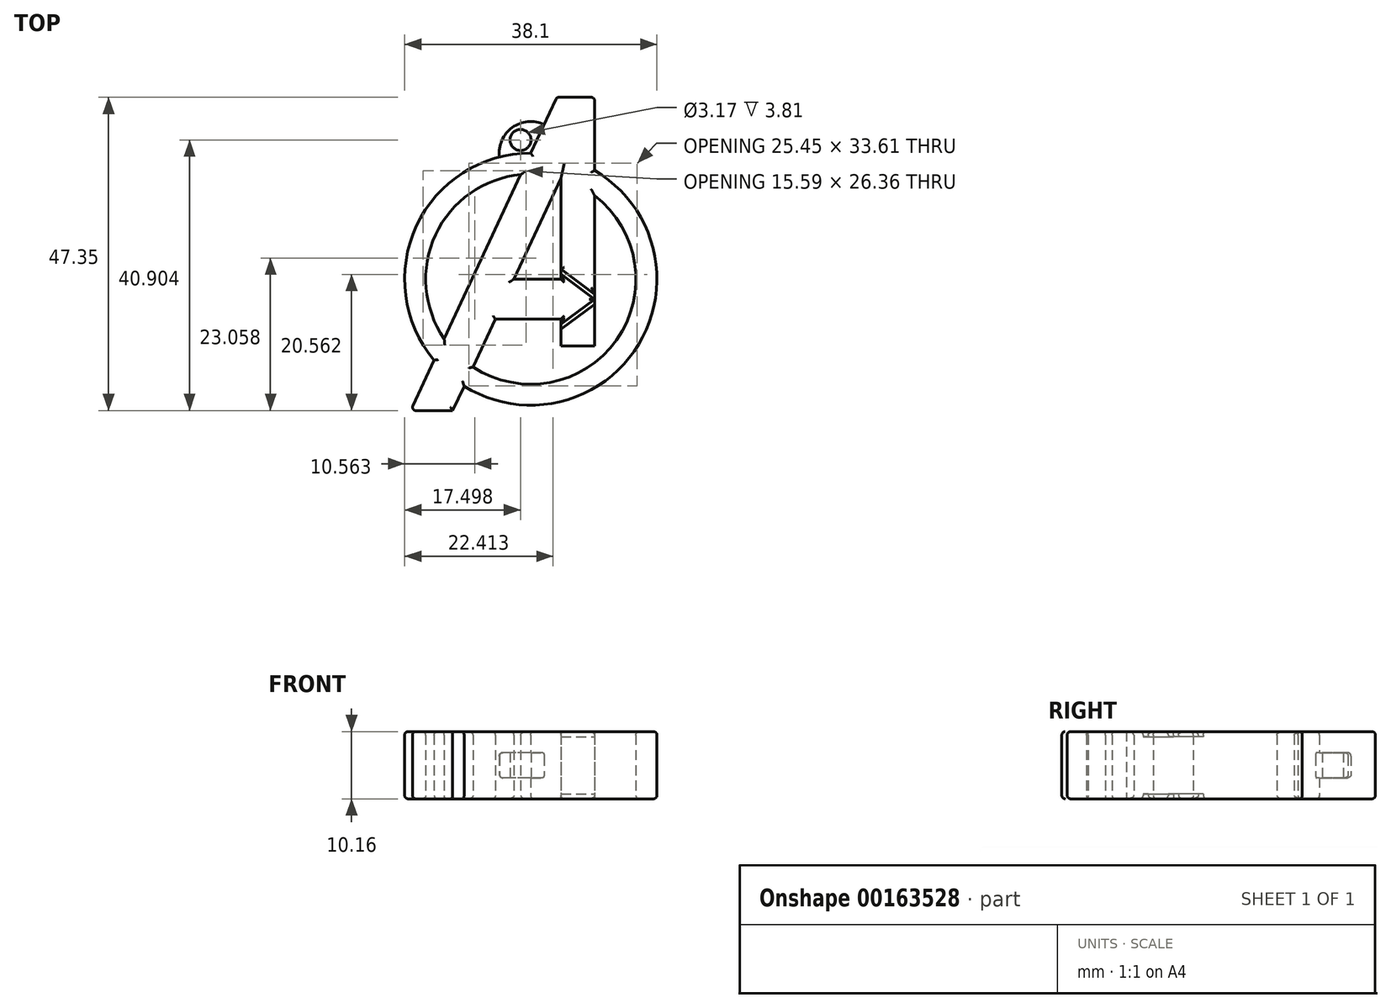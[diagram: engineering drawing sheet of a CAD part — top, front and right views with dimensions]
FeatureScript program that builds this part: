
annotation { "Feature Type Name" : "Feature", "Feature Type Description" : "" }
export const myFeature = defineFeature(function(context is Context, id is Id, definition is map)
    precondition{}
    {
        {
            var Q0;
            Q0=qCreatedBy(makeId("Top.planeOp"),FACE);
            var sketch = newSketch(context, id + "F0", { "sketchPlane" : qUnion([Q0])});
            skArc(sketch, "E0", {"start": v(0, 19.05) * mm, "mid": v(-17.27, 8.05) * mm, "end": v(-14.6, -12.25) * mm});
            skArc(sketch, "E1", {"start": v(-1.51, 15.8) * mm, "mid": v(-14.39, 6.7) * mm, "end": v(-13.08, -9) * mm});
            skLineSegment(sketch, "E2", {"start": v(0, 19.05) * mm, "end": v(-18.15, -19.87) * mm});
            skLineSegment(sketch, "E3", {"start": v(-18.15, -19.87) * mm, "end": v(-11.8, -19.87) * mm});
            skLineSegment(sketch, "E4", {"start": v(-11.8, -19.87) * mm, "end": v(-5.36, -6.05) * mm});
            skLineSegment(sketch, "E5", {"start": v(4.56, 15.2) * mm, "end": v(4.56, 0) * mm});
            skLineSegment(sketch, "E6", {"start": v(4.56, -10.12) * mm, "end": v(9.64, -10.12) * mm});
            skLineSegment(sketch, "E7", {"start": v(-14.6, -12.25) * mm, "end": v(-18.15, -19.87) * mm});
            skLineSegment(sketch, "E8", {"start": v(9.64, 12.61) * mm, "end": v(9.64, 27.48) * mm});
            skLineSegment(sketch, "E9", {"start": v(0, 19.05) * mm, "end": v(3.93, 27.48) * mm});
            skLineSegment(sketch, "E10", {"start": v(9.64, 27.48) * mm, "end": v(3.93, 27.48) * mm});
            skLineSegment(sketch, "E11", {"start": v(-5.36, -6.05) * mm, "end": v(4.56, -6.05) * mm});
            skLineSegment(sketch, "E12", {"start": v(-2.53, 0) * mm, "end": v(4.56, 0) * mm});
            skLineSegment(sketch, "E13.trimOffspring", {"start": v(4.56, -6.05) * mm, "end": v(4.56, -10.12) * mm});
            skLineSegment(sketch, "E14.trimOffspring", {"start": v(-2.53, 0) * mm, "end": v(4.56, 15.2) * mm});
            skArc(sketch, "E15.trimOffspring", {"start": v(-8.72, -13.27) * mm, "mid": v(12.95, -9.18) * mm, "end": v(9.64, 12.61) * mm});
            skArc(sketch, "E16.trimOffspring", {"start": v(-10.07, -16.17) * mm, "mid": v(16.3, -9.86) * mm, "end": v(9.64, 16.43) * mm});
            skArc(sketch, "E17", {"start": v(2.01, 23.37) * mm, "mid": v(-2.8, 22.9) * mm, "end": v(-4.73, 18.45) * mm});
            skCircle(sketch, "E18", {"center": v(-1.55, 21.03) * mm, "radius": 1.59 * mm});
            skLineSegment(sketch, "E19", {"start": v(4.56, 0) * mm, "end": v(4.56, 0.76) * mm});
            skLineSegment(sketch, "E20", {"start": v(4.56, 0.76) * mm, "end": v(4.56, 1.52) * mm});
            skLineSegment(sketch, "E21", {"start": v(4.56, -6.05) * mm, "end": v(4.56, -6.81) * mm});
            skLineSegment(sketch, "E22", {"start": v(4.56, -6.81) * mm, "end": v(4.56, -7.58) * mm});
            skLineSegment(sketch, "E23", {"start": v(4.56, 0.76) * mm, "end": v(9.64, -3.03) * mm});
            skLineSegment(sketch, "E24", {"start": v(4.56, -6.81) * mm, "end": v(9.64, -3.03) * mm});
            skLineSegment(sketch, "E25", {"start": v(4.56, 1.52) * mm, "end": v(9.64, -2.26) * mm});
            skLineSegment(sketch, "E26", {"start": v(4.56, -7.58) * mm, "end": v(9.64, -3.79) * mm});
            skPoint(sketch, "E27.trimOffspring.start.orphan", {"position": v(9.64, -6.05) * mm});
            skPoint(sketch, "E28.end.orphan", {"position": v(9.64, 0) * mm});
            skLineSegment(sketch, "E29", {"start": v(9.64, 12.61) * mm, "end": v(9.64, -10.12) * mm});
            skLineSegment(sketch, "E30", {"start": v(4.56, 1.14) * mm, "end": v(9.64, -2.65) * mm});
            skLineSegment(sketch, "E31", {"start": v(4.56, -7.2) * mm, "end": v(9.64, -3.4) * mm});
            skLineSegment(sketch, "E32", {"start": v(-11.8, -19.87) * mm, "end": v(25.13, -19.87) * mm});
            skLineSegment(sketch, "E33", {"start": v(9.64, 27.48) * mm, "end": v(25.13, 27.48) * mm});
            skLineSegment(sketch, "E34", {"start": v(25.13, 27.48) * mm, "end": v(25.13, -19.87) * mm});
            skLineSegment(sketch, "E35", {"start": v(-19.05, 0) * mm, "end": v(-19.05, -24.18) * mm});
            skLineSegment(sketch, "E36", {"start": v(-19.05, -24.18) * mm, "end": v(19.05, -24.18) * mm});
            skLineSegment(sketch, "E37", {"start": v(19.05, 0) * mm, "end": v(19.05, -24.18) * mm});
            skSolve(sketch);
        }
        {
            var Q0;
            {var subQ2=sQuery(id+"F0.wireOp",EDGE,"E0");Q0=makeQuery(id+"F0.imprint","IMPRINT",FACE,{"disambiguationData":[TD([[makeQuery(id+"F0.imprint","IMPRINT",EDGE,{"derivedFrom":subQ2}),1.0]])]});}
            var Q1;
            {var subQ9=sQuery(id+"F0.wireOp",EDGE,"E3");Q1=makeQuery(id+"F0.imprint","IMPRINT",FACE,{"disambiguationData":[TD([[makeQuery(id+"F0.imprint","IMPRINT",EDGE,{"derivedFrom":subQ9}),1.0]])]});}
            var Q2;
            {var subQ0=sQuery(id+"F0.wireOp",EDGE,"E15.trimOffspring");Q2=makeQuery(id+"F0.imprint","IMPRINT",FACE,{"disambiguationData":[TD([[makeQuery(id+"F0.imprint","IMPRINT",EDGE,{"derivedFrom":subQ0}),-1.0]])]});}
            var Q3;
            Q3=makeQuery(id+"F0.imprint","IMPRINT",FACE,{"disambiguationData":[TD([[makeQuery(id+"F0.imprint","IMPRINT",EDGE,{"derivedFrom":sQuery(id+"F0.wireOp",EDGE,"E6")}),1.0]])]});
            var Q4;
            {var subQ1=sQuery(id+"F0.wireOp",EDGE,"406db947-73c3-418f-ad74-710f48655b45");Q4=makeQuery(id+"F0.imprint","IMPRINT",FACE,{"disambiguationData":[TD([[makeQuery(id+"F0.imprint","IMPRINT",EDGE,{"derivedFrom":subQ1}),-1.0]])]});}
            var Q5;
            {var subQ2=sQuery(id+"F0.wireOp",EDGE,"08405404-7948-4caf-93e0-b9b2559490a3");Q5=makeQuery(id+"F0.imprint","IMPRINT",FACE,{"disambiguationData":[TD([[makeQuery(id+"F0.imprint","IMPRINT",EDGE,{"derivedFrom":subQ2}),1.0]])]});}
            var Q6;
            {var subQ2=sQuery(id+"F0.wireOp",EDGE,"49d6b685-f15b-4148-abe2-4aacc5afd56f");Q6=makeQuery(id+"F0.imprint","IMPRINT",FACE,{"disambiguationData":[TD([[makeQuery(id+"F0.imprint","IMPRINT",EDGE,{"derivedFrom":subQ2}),1.0]])]});}
            var Q7;
            {var subQ2=sQuery(id+"F0.wireOp",EDGE,"e047c4b4-439f-4a13-8362-1945e49fde9b");Q7=makeQuery(id+"F0.imprint","IMPRINT",FACE,{"disambiguationData":[TD([[makeQuery(id+"F0.imprint","IMPRINT",EDGE,{"derivedFrom":subQ2}),1.0]])]});}
            extrude(context, id + "F1", {"entities" : qUnion([Q0, Q1, Q2, Q3, Q4, Q5, Q6, Q7]), "depth" : 5.08 * mm});
        }
        {
            var Q0;
            {var subQ1=sQuery(id+"F0.wireOp",EDGE,"E15.trimOffspring");Q0=makeQuery(id+"F0.imprint","IMPRINT",FACE,{"disambiguationData":[TD([[makeQuery(id+"F0.imprint","IMPRINT",EDGE,{"derivedFrom":subQ1}),-1.0]])]});}
            var Q1;
            {var subQ1=sQuery(id+"F0.wireOp",EDGE,"E1");Q1=makeQuery(id+"F0.imprint","IMPRINT",FACE,{"disambiguationData":[TD([[makeQuery(id+"F0.imprint","IMPRINT",EDGE,{"derivedFrom":subQ1}),-1.0]])]});}
            var Q2;
            {var subQ9=sQuery(id+"F0.wireOp",EDGE,"E3");Q2=makeQuery(id+"F0.imprint","IMPRINT",FACE,{"disambiguationData":[TD([[makeQuery(id+"F0.imprint","IMPRINT",EDGE,{"derivedFrom":subQ9}),1.0]])]});}
            var Q3;
            {var subQ2=sQuery(id+"F0.wireOp",EDGE,"E6");Q3=makeQuery(id+"F0.imprint","IMPRINT",FACE,{"disambiguationData":[TD([[makeQuery(id+"F0.imprint","IMPRINT",EDGE,{"derivedFrom":subQ2}),1.0]])]});}
            extrude(context, id + "F2", {"entities" : qUnion([Q0, Q1, Q2, Q3]), "operationType" : NewBodyOperationType.ADD, "oppositeDirection" : true, "depth" : 5.08 * mm});
        }
        {
            var Q0;
            {var subQ0=sQuery(id+"F0.wireOp",EDGE,"E17");Q0=makeQuery(id+"F0.imprint","IMPRINT",FACE,{"disambiguationData":[TD([[makeQuery(id+"F0.imprint","IMPRINT",EDGE,{"derivedFrom":subQ0}),1.0]])]});}
            extrude(context, id + "F3", {"entities" : qUnion([Q0]), "operationType" : NewBodyOperationType.ADD, "depth" : 1.9 * mm});
        }
        {
            var Q0;
            {var subQ0=sQuery(id+"F0.wireOp",EDGE,"E17");Q0=makeQuery(id+"F0.imprint","IMPRINT",FACE,{"disambiguationData":[TD([[makeQuery(id+"F0.imprint","IMPRINT",EDGE,{"derivedFrom":subQ0}),1.0]])]});}
            extrude(context, id + "F4", {"entities" : qUnion([Q0]), "operationType" : NewBodyOperationType.ADD, "oppositeDirection" : true, "depth" : 1.9 * mm});
        }
        {
            var Q0;
            {var subQ2=sQuery(id+"F0.wireOp",EDGE,"E25");Q0=makeQuery(id+"F0.imprint","IMPRINT",FACE,{"disambiguationData":[TD([[makeQuery(id+"F0.imprint","IMPRINT",EDGE,{"derivedFrom":subQ2}),-1.0]])]});}
            var Q1;
            {var subQ2=sQuery(id+"F0.wireOp",EDGE,"E23");Q1=makeQuery(id+"F0.imprint","IMPRINT",FACE,{"disambiguationData":[TD([[makeQuery(id+"F0.imprint","IMPRINT",EDGE,{"derivedFrom":subQ2}),1.0]])]});}
            var Q2;
            {var subQ2=sQuery(id+"F0.wireOp",EDGE,"E24");Q2=makeQuery(id+"F0.imprint","IMPRINT",FACE,{"disambiguationData":[TD([[makeQuery(id+"F0.imprint","IMPRINT",EDGE,{"derivedFrom":subQ2}),-1.0]])]});}
            var Q3;
            {var subQ2=sQuery(id+"F0.wireOp",EDGE,"E26");Q3=makeQuery(id+"F0.imprint","IMPRINT",FACE,{"disambiguationData":[TD([[makeQuery(id+"F0.imprint","IMPRINT",EDGE,{"derivedFrom":subQ2}),1.0]])]});}
            extrude(context, id + "F5", {"entities" : qUnion([Q0, Q1, Q2, Q3]), "operationType" : NewBodyOperationType.ADD, "depth" : 4.32 * mm});
        }
        {
            var Q0;
            {var subQ2=sQuery(id+"F0.wireOp",EDGE,"E23");Q0=makeQuery(id+"F0.imprint","IMPRINT",FACE,{"disambiguationData":[TD([[makeQuery(id+"F0.imprint","IMPRINT",EDGE,{"derivedFrom":subQ2}),1.0]])]});}
            var Q1;
            {var subQ2=sQuery(id+"F0.wireOp",EDGE,"E25");Q1=makeQuery(id+"F0.imprint","IMPRINT",FACE,{"disambiguationData":[TD([[makeQuery(id+"F0.imprint","IMPRINT",EDGE,{"derivedFrom":subQ2}),-1.0]])]});}
            var Q2;
            {var subQ2=sQuery(id+"F0.wireOp",EDGE,"E24");Q2=makeQuery(id+"F0.imprint","IMPRINT",FACE,{"disambiguationData":[TD([[makeQuery(id+"F0.imprint","IMPRINT",EDGE,{"derivedFrom":subQ2}),-1.0]])]});}
            var Q3;
            {var subQ2=sQuery(id+"F0.wireOp",EDGE,"E26");Q3=makeQuery(id+"F0.imprint","IMPRINT",FACE,{"disambiguationData":[TD([[makeQuery(id+"F0.imprint","IMPRINT",EDGE,{"derivedFrom":subQ2}),1.0]])]});}
            extrude(context, id + "F6", {"entities" : qUnion([Q0, Q1, Q2, Q3]), "operationType" : NewBodyOperationType.ADD, "oppositeDirection" : true, "depth" : 4.32 * mm});
        }
        {
            var Q0;
            Q0=makeQuery(id+"F3.opExtrude","CAP_EDGE",EDGE,{"disambiguationData":[OSD([sQuery(id+"F0.wireOp",EDGE,"E17")])],"isStart":false});
            var Q1;
            Q1=makeQuery(id+"F4.opExtrude","CAP_EDGE",EDGE,{"disambiguationData":[OSD([sQuery(id+"F0.wireOp",EDGE,"E17")])],"isStart":false});
            var Q2;
            Q2=makeQuery(id+"F2.opExtrude","CAP_EDGE",EDGE,{"disambiguationData":[OSD([sQuery(id+"F0.wireOp",EDGE,"E9")])],"isStart":false});
            var Q3;
            Q3=makeQuery(id+"F1.opExtrude","CAP_EDGE",EDGE,{"disambiguationData":[OSD([sQuery(id+"F0.wireOp",EDGE,"E9")])],"isStart":false});
            var Q4;
            Q4=makeQuery(id+"F2.opExtrude","CAP_EDGE",EDGE,{"disambiguationData":[OSD([sQuery(id+"F0.wireOp",EDGE,"E0")])],"isStart":false});
            var Q5;
            Q5=makeQuery(id+"F1.opExtrude","CAP_EDGE",EDGE,{"disambiguationData":[OSD([sQuery(id+"F0.wireOp",EDGE,"E0")])],"isStart":false});
            var Q6;
            Q6=makeQuery(id+"F2.opExtrude","CAP_EDGE",EDGE,{"disambiguationData":[OSD([sQuery(id+"F0.wireOp",EDGE,"E7")])],"isStart":false});
            var Q7;
            Q7=makeQuery(id+"F1.opExtrude","CAP_EDGE",EDGE,{"disambiguationData":[OSD([sQuery(id+"F0.wireOp",EDGE,"E7")])],"isStart":false});
            var Q8;
            {var subQ0=sQuery(id+"F0.wireOp",EDGE,"E3");var subQ1=sQuery(id+"F0.wireOp",EDGE,"E7");Q8=makeQuery(id+"F2.boolean.opBoolean","MERGE",EDGE,{"derivedFrom":[makeQuery(id+"F1.opExtrude","SWEPT_EDGE",EDGE,{"disambiguationData":[OSD([subQ0,subQ1])]}),makeQuery(id+"F2.opExtrude","SWEPT_EDGE",EDGE,{"disambiguationData":[OSD([subQ0,subQ1])]})]});}
            var Q9;
            Q9=makeQuery(id+"F1.opExtrude","CAP_EDGE",EDGE,{"disambiguationData":[OSD([sQuery(id+"F0.wireOp",EDGE,"E3")])],"isStart":false});
            var Q10;
            {var subQ0=sQuery(id+"F0.wireOp",EDGE,"E3");var subQ1=sQuery(id+"F0.wireOp",EDGE,"E4");Q10=makeQuery(id+"F2.boolean.opBoolean","MERGE",EDGE,{"derivedFrom":[makeQuery(id+"F1.opExtrude","SWEPT_EDGE",EDGE,{"disambiguationData":[OSD([subQ0,subQ1])]}),makeQuery(id+"F2.opExtrude","SWEPT_EDGE",EDGE,{"disambiguationData":[OSD([subQ0,subQ1])]})]});}
            var Q11;
            Q11=makeQuery(id+"F2.opExtrude","CAP_EDGE",EDGE,{"disambiguationData":[OSD([sQuery(id+"F0.wireOp",EDGE,"E3")])],"isStart":false});
            var Q12;
            {var subQ0=sQuery(id+"F0.wireOp",EDGE,"E4");Q12=makeQuery(id+"F2.opExtrude","CAP_EDGE",EDGE,{"disambiguationData":[OSD([subQ0]),TDD([makeQuery(id+"F0.imprint","IMPRINT",EDGE,{"disambiguationData":[TD([[makeQuery(id+"F0.imprint","INTERSECT",VERTEX,{"derivedFrom":[sQuery(id+"F0.wireOp",EDGE,"E3"),subQ0]}),-1.0]])],"derivedFrom":subQ0})])],"isStart":false});}
            var Q13;
            {var subQ0=sQuery(id+"F0.wireOp",EDGE,"E4");Q13=makeQuery(id+"F1.opExtrude","CAP_EDGE",EDGE,{"disambiguationData":[OSD([subQ0]),TDD([makeQuery(id+"F0.imprint","IMPRINT",EDGE,{"disambiguationData":[TD([[makeQuery(id+"F0.imprint","INTERSECT",VERTEX,{"derivedFrom":[sQuery(id+"F0.wireOp",EDGE,"E3"),subQ0]}),-1.0]])],"derivedFrom":subQ0})])],"isStart":false});}
            var Q14;
            Q14=makeQuery(id+"F1.opExtrude","CAP_EDGE",EDGE,{"disambiguationData":[OSD([sQuery(id+"F0.wireOp",EDGE,"E16.trimOffspring")])],"isStart":false});
            var Q15;
            Q15=makeQuery(id+"F2.opExtrude","CAP_FACE",FACE,{"disambiguationData":[OSD([sQuery(id+"F0.wireOp",EDGE,"E0"),sQuery(id+"F0.wireOp",EDGE,"E1"),sQuery(id+"F0.wireOp",EDGE,"E2"),sQuery(id+"F0.wireOp",EDGE,"E3"),sQuery(id+"F0.wireOp",EDGE,"E5"),sQuery(id+"F0.wireOp",EDGE,"E7"),sQuery(id+"F0.wireOp",EDGE,"E8"),sQuery(id+"F0.wireOp",EDGE,"E9"),sQuery(id+"F0.wireOp",EDGE,"E10"),sQuery(id+"F0.wireOp",EDGE,"E4"),sQuery(id+"F0.wireOp",EDGE,"E11"),sQuery(id+"F0.wireOp",EDGE,"E12"),sQuery(id+"F0.wireOp",EDGE,"E14.trimOffspring"),sQuery(id+"F0.wireOp",EDGE,"E15.trimOffspring"),sQuery(id+"F0.wireOp",EDGE,"E16.trimOffspring"),sQuery(id+"F0.wireOp",EDGE,"E19"),sQuery(id+"F0.wireOp",EDGE,"E21"),sQuery(id+"F0.wireOp",EDGE,"E23"),sQuery(id+"F0.wireOp",EDGE,"E24"),sQuery(id+"F0.wireOp",EDGE,"E25"),sQuery(id+"F0.wireOp",EDGE,"E29")])],"isStart":false});
            var Q16;
            Q16=makeQuery(id+"F2.opExtrude","CAP_EDGE",EDGE,{"disambiguationData":[OSD([sQuery(id+"F0.wireOp",EDGE,"E16.trimOffspring")])],"isStart":false});
            var Q17;
            {var subQ0=sQuery(id+"F0.wireOp",EDGE,"E8");var subQ1=sQuery(id+"F0.wireOp",EDGE,"E10");Q17=makeQuery(id+"F2.boolean.opBoolean","MERGE",EDGE,{"derivedFrom":[makeQuery(id+"F1.opExtrude","SWEPT_EDGE",EDGE,{"disambiguationData":[OSD([subQ0,subQ1])]}),makeQuery(id+"F2.opExtrude","SWEPT_EDGE",EDGE,{"disambiguationData":[OSD([subQ0,subQ1])]})]});}
            var Q18;
            Q18=makeQuery(id+"F2.opExtrude","CAP_EDGE",EDGE,{"disambiguationData":[OSD([sQuery(id+"F0.wireOp",EDGE,"E8")])],"isStart":false});
            var Q19;
            Q19=makeQuery(id+"F1.opExtrude","CAP_EDGE",EDGE,{"disambiguationData":[OSD([sQuery(id+"F0.wireOp",EDGE,"E8")])],"isStart":false});
            var Q20;
            {var subQ0=sQuery(id+"F0.wireOp",EDGE,"E9");var subQ1=sQuery(id+"F0.wireOp",EDGE,"E10");Q20=makeQuery(id+"F2.boolean.opBoolean","MERGE",EDGE,{"derivedFrom":[makeQuery(id+"F1.opExtrude","SWEPT_EDGE",EDGE,{"disambiguationData":[OSD([subQ0,subQ1])]}),makeQuery(id+"F2.opExtrude","SWEPT_EDGE",EDGE,{"disambiguationData":[OSD([subQ0,subQ1])]})]});}
            var Q21;
            Q21=makeQuery(id+"F1.opExtrude","CAP_FACE",FACE,{"disambiguationData":[OSD([sQuery(id+"F0.wireOp",EDGE,"E0"),sQuery(id+"F0.wireOp",EDGE,"E1"),sQuery(id+"F0.wireOp",EDGE,"E2"),sQuery(id+"F0.wireOp",EDGE,"E3"),sQuery(id+"F0.wireOp",EDGE,"E5"),sQuery(id+"F0.wireOp",EDGE,"E7"),sQuery(id+"F0.wireOp",EDGE,"E8"),sQuery(id+"F0.wireOp",EDGE,"E9"),sQuery(id+"F0.wireOp",EDGE,"E10"),sQuery(id+"F0.wireOp",EDGE,"E4"),sQuery(id+"F0.wireOp",EDGE,"E11"),sQuery(id+"F0.wireOp",EDGE,"E12"),sQuery(id+"F0.wireOp",EDGE,"E14.trimOffspring"),sQuery(id+"F0.wireOp",EDGE,"E15.trimOffspring"),sQuery(id+"F0.wireOp",EDGE,"E16.trimOffspring"),sQuery(id+"F0.wireOp",EDGE,"E19"),sQuery(id+"F0.wireOp",EDGE,"E21"),sQuery(id+"F0.wireOp",EDGE,"E23"),sQuery(id+"F0.wireOp",EDGE,"E24"),sQuery(id+"F0.wireOp",EDGE,"E25"),sQuery(id+"F0.wireOp",EDGE,"E29")])],"isStart":false});
            var Q22;
            Q22=makeQuery(id+"F1.opExtrude","CAP_EDGE",EDGE,{"disambiguationData":[OSD([sQuery(id+"F0.wireOp",EDGE,"E26")])],"isStart":false});
            var Q23;
            Q23=makeQuery(id+"F2.opExtrude","CAP_EDGE",EDGE,{"disambiguationData":[OSD([sQuery(id+"F0.wireOp",EDGE,"E26")])],"isStart":false});
            fillet(context, id + "F7", {"entities" : qUnion([Q0, Q1, Q2, Q3, Q4, Q5, Q6, Q7, Q8, Q9, Q10, Q11, Q12, Q13, Q14, Q15, Q16, Q17, Q18, Q19, Q20, Q21, Q22, Q23]), "radius" : 0.5 * mm, "tangentPropagation" : true, "allowEdgeOverflow" : false});
        }
    });
